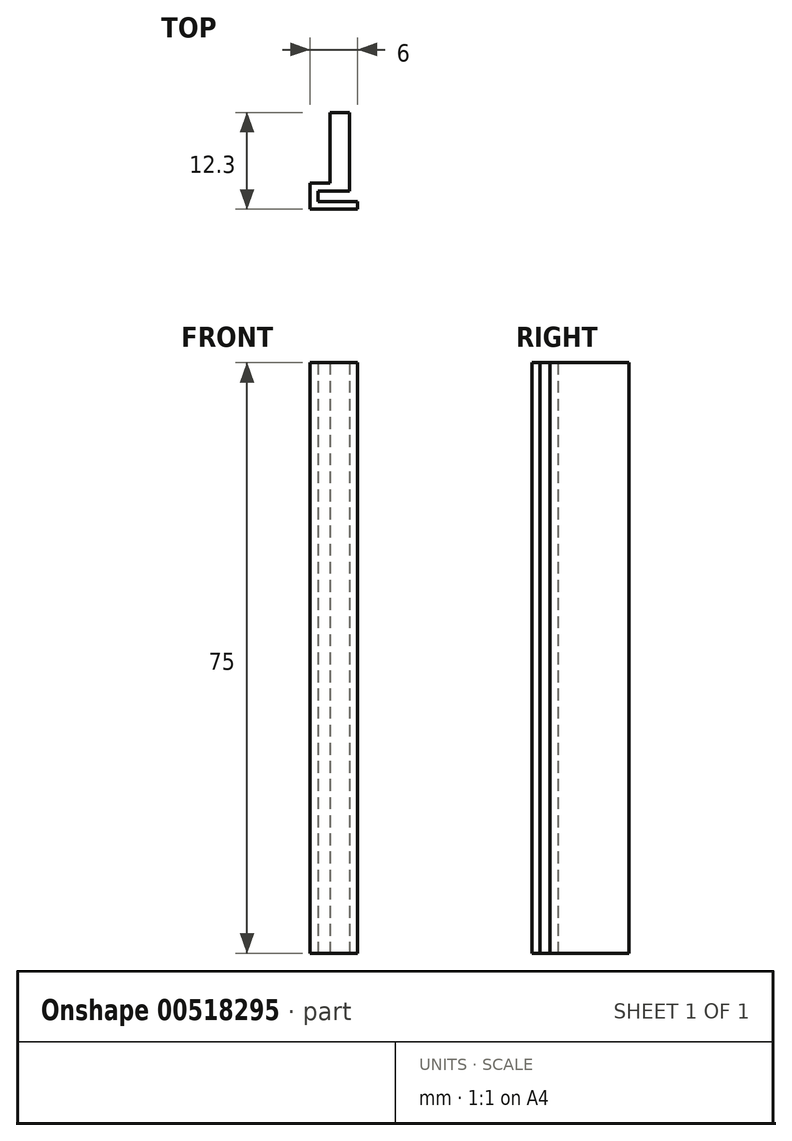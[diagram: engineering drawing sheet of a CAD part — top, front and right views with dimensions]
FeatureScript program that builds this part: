
annotation { "Feature Type Name" : "Feature", "Feature Type Description" : "" }
export const myFeature = defineFeature(function(context is Context, id is Id, definition is map)
    precondition{}
    {
        {
            var Q0;
            Q0=qCreatedBy(makeId("Top.planeOp"),FACE);
            var sketch = newSketch(context, id + "F0", { "sketchPlane" : qUnion([Q0])});
            skLineSegment(sketch, "E0", {"start": v(5, 10) * mm, "end": v(5, 0) * mm});
            skLineSegment(sketch, "E1", {"start": v(5, 0) * mm, "end": v(1, 0) * mm});
            skLineSegment(sketch, "E2", {"start": v(1, 0) * mm, "end": v(1, -1.3) * mm});
            skLineSegment(sketch, "E3", {"start": v(1, -1.3) * mm, "end": v(6, -1.3) * mm});
            skLineSegment(sketch, "E4", {"start": v(6, -1.3) * mm, "end": v(6, -2.3) * mm});
            skLineSegment(sketch, "E5", {"start": v(6, -2.3) * mm, "end": v(0, -2.3) * mm});
            skLineSegment(sketch, "E6", {"start": v(0, -2.3) * mm, "end": v(0, 0) * mm});
            skLineSegment(sketch, "E7", {"start": v(0, 0) * mm, "end": v(0, 1) * mm});
            skLineSegment(sketch, "E8", {"start": v(0, 1) * mm, "end": v(2.5, 1) * mm});
            skLineSegment(sketch, "E9", {"start": v(2.5, 1) * mm, "end": v(2.5, 10) * mm});
            skLineSegment(sketch, "E10", {"start": v(2.5, 10) * mm, "end": v(5, 10) * mm});
            skSolve(sketch);
        }
        {
            var Q0;
            Q0 = qSketchRegion(id + "F0", true);
            extrude(context, id + "F1", {"entities" : qUnion([Q0]), "depth" : 75 * mm, "offsetDistance" : 25 * mm});
        }
    });
